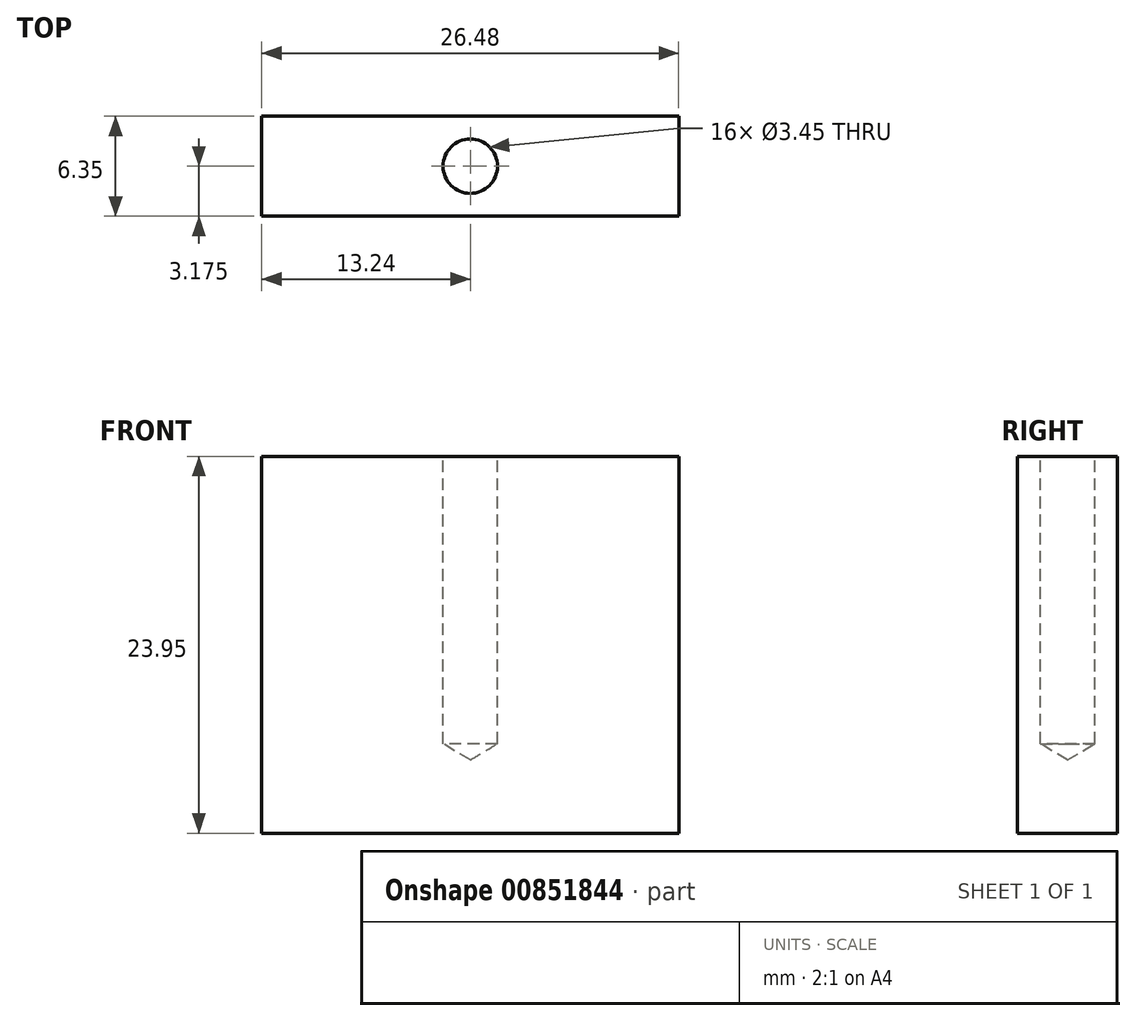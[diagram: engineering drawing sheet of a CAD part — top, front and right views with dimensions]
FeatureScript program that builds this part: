
annotation { "Feature Type Name" : "Feature", "Feature Type Description" : "" }
export const myFeature = defineFeature(function(context is Context, id is Id, definition is map)
    precondition{}
    {
        {
            var Q0;
            Q0=qCreatedBy(makeId("Front.planeOp"),FACE);
            var sketch = newSketch(context, id + "F0", { "sketchPlane" : qUnion([Q0])});
            skLineSegment(sketch, "E0.bottom", {"start": v(-11.13, 15.03) * mm, "end": v(15.35, 15.03) * mm});
            skLineSegment(sketch, "E0.top", {"start": v(-11.13, -8.92) * mm, "end": v(15.35, -8.92) * mm});
            skLineSegment(sketch, "E0.left", {"start": v(-11.13, 15.03) * mm, "end": v(-11.13, -8.92) * mm});
            skLineSegment(sketch, "E0.right", {"start": v(15.35, 15.03) * mm, "end": v(15.35, -8.92) * mm});
            skSolve(sketch);
        }
        {
            var Q0;
            Q0=makeQuery(id+"F0.imprint","IMPRINT",FACE,{"disambiguationData":[TD([[makeQuery(id+"F0.imprint","IMPRINT",EDGE,{"derivedFrom":sQuery(id+"F0.wireOp",EDGE,"E0.bottom")}),-1.0]])]});
            extrude(context, id + "F1", {"entities" : qUnion([Q0]), "depth" : 6.35 * mm, "offsetDistance" : 25.4 * mm});
        }
        {
            var Q0;
            Q0=makeQuery(id+"F1.opExtrude","SWEPT_FACE",FACE,{"disambiguationData":[OSD([sQuery(id+"F0.wireOp",EDGE,"E0.bottom")])]});
            var sketch = newSketch(context, id + "F2", { "sketchPlane" : qUnion([Q0])});
            skLineSegment(sketch, "E1", {"start": v(2.11, -6.35) * mm, "end": v(2.11, 0) * mm});
            skPoint(sketch, "E2", {"position": v(2.11, -3.18) * mm});
            skSolve(sketch);
        }
        {
            var Q0;
            Q0=sQuery(id+"F2.wireOp",VERTEX,"E2");
            var Q1;
            Q1=makeQuery(id+"F1.opExtrude","SWEPT_BODY",BODY,{"disambiguationData":[OSD([sQuery(id+"F0.wireOp",EDGE,"E0.bottom"),sQuery(id+"F0.wireOp",EDGE,"E0.top"),sQuery(id+"F0.wireOp",EDGE,"E0.left"),sQuery(id+"F0.wireOp",EDGE,"E0.right")])]});
            hole(context, id + "F3", {"style" : HoleStyle.SIMPLE, "endStyle" : HoleEndStyle.BLIND, "standardTappedOrClearance" : lookupTablePath({ "standard" : "ANSI", "engagement" : "75%", "pitch" : "32 tpi", "size" : "#8", "type" : "Tapped" }), "standardBlindInLast" : lookupTablePath({ "standard" : "ANSI", "engagement" : "75%", "pitch" : "32 tpi", "size" : "#8", "type" : "Tapped" }), "holeDiameter" : 3.45 * mm, "majorDiameter" : 4.17 * mm, "showTappedDepth" : true, "holeDepth" : 18.26 * mm, "isTappedThrough" : true, "tappedDepth" : 15.88 * mm, "tapClearance" : 3, "locations" : qUnion([Q0]), "scope" : qUnion([Q1])});
        }
    });
